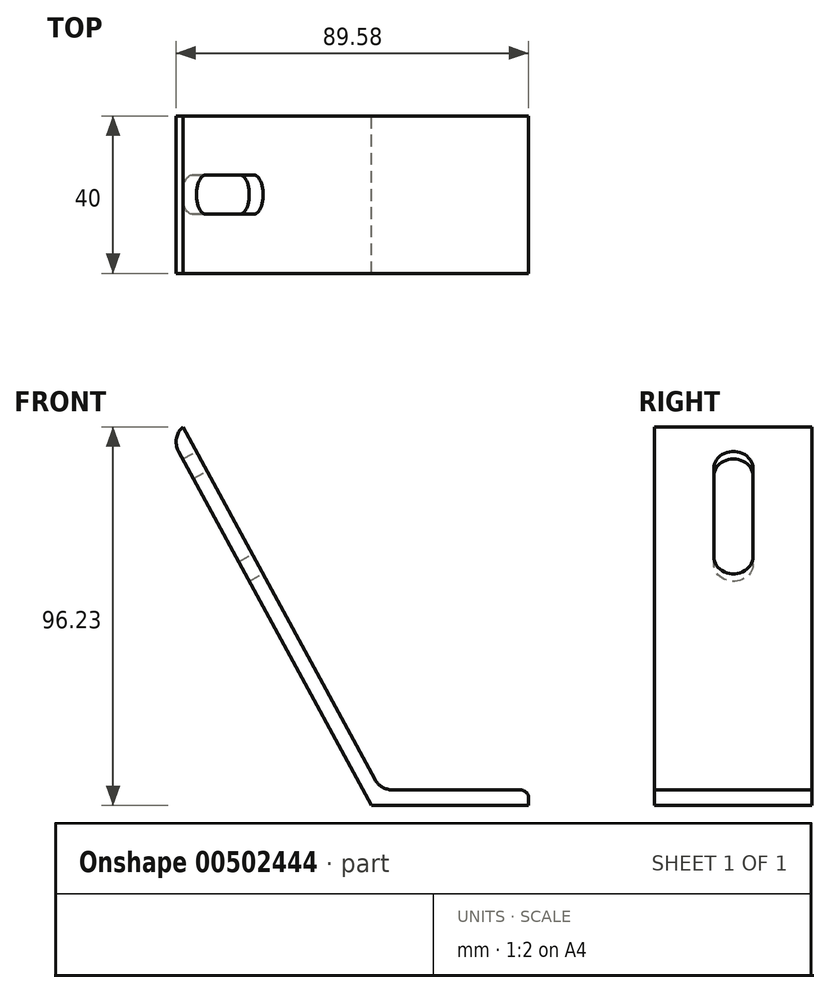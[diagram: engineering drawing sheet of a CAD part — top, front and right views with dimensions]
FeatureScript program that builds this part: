
annotation { "Feature Type Name" : "Feature", "Feature Type Description" : "" }
export const myFeature = defineFeature(function(context is Context, id is Id, definition is map)
    precondition{}
    {
        {
            var Q0;
            Q0=qCreatedBy(makeId("Front.planeOp"),FACE);
            var sketch = newSketch(context, id + "F0", { "sketchPlane" : qUnion([Q0])});
            skLineSegment(sketch, "E0", {"start": v(-3, 5.51) * mm, "end": v(-51.31, 94.32) * mm});
            skLineSegment(sketch, "E1", {"start": v(-51.31, 94.32) * mm, "end": v(-47.8, 96.23) * mm});
            skLineSegment(sketch, "E2", {"start": v(-47.8, 96.23) * mm, "end": v(2.38, 4) * mm});
            skLineSegment(sketch, "E3", {"start": v(2.38, 4) * mm, "end": v(40, 4) * mm});
            skLineSegment(sketch, "E4", {"start": v(40, 4) * mm, "end": v(40, 0) * mm});
            skLineSegment(sketch, "E5", {"start": v(40, 0) * mm, "end": v(0, 0) * mm});
            skLineSegment(sketch, "E6", {"start": v(0, 0) * mm, "end": v(-3, 5.51) * mm});
            skSolve(sketch);
        }
        {
            var Q0;
            Q0 = qSketchRegion(id + "F0", true);
            extrude(context, id + "F1", {"entities" : qUnion([Q0]), "depth" : 40 * mm});
        }
        {
            var Q0;
            Q0=makeQuery(id+"F1.opExtrude","SWEPT_EDGE",EDGE,{"disambiguationData":[OSD([sQuery(id+"F0.wireOp",EDGE,"E2"),sQuery(id+"F0.wireOp",EDGE,"E3")])]});
            var Q1;
            Q1=makeQuery(id+"F1.opExtrude","SWEPT_EDGE",EDGE,{"disambiguationData":[OSD([sQuery(id+"F0.wireOp",EDGE,"E0"),sQuery(id+"F0.wireOp",EDGE,"AraJsjXW-HaTJ-uxDT-Rq7w-RD12DYAYVZGL")])]});
            fillet(context, id + "F2", {"entities" : qUnion([Q0, Q1]), "radius" : 5 * mm, "tangentPropagation" : true, "allowEdgeOverflow" : false});
        }
        {
            var Q0;
            Q0=makeQuery(id+"F1.opExtrude","SWEPT_EDGE",EDGE,{"disambiguationData":[OSD([sQuery(id+"F0.wireOp",EDGE,"E3"),sQuery(id+"F0.wireOp",EDGE,"E4")])]});
            var Q1;
            Q1=makeQuery(id+"F1.opExtrude","SWEPT_EDGE",EDGE,{"disambiguationData":[OSD([sQuery(id+"F0.wireOp",EDGE,"jgJGadt5-KIKr-K8Ni-Qctq-57nrNfer92To"),sQuery(id+"F0.wireOp",EDGE,"jqPTAw02-jaw2-K15B-pJJS-fNdpXxf2ybxW")])]});
            var Q2;
            Q2=makeQuery(id+"F1.opExtrude","SWEPT_EDGE",EDGE,{"disambiguationData":[OSD([sQuery(id+"F0.wireOp",EDGE,"wX90dwEU-SlRl-KfoV-YeP7-xEuWKFcL9DTf"),sQuery(id+"F0.wireOp",EDGE,"AraJsjXW-HaTJ-uxDT-Rq7w-RD12DYAYVZGL")])]});
            var Q3;
            Q3=makeQuery(id+"F1.opExtrude","SWEPT_EDGE",EDGE,{"disambiguationData":[OSD([sQuery(id+"F0.wireOp",EDGE,"E1"),sQuery(id+"F0.wireOp",EDGE,"E2")])]});
            var Q4;
            Q4=makeQuery(id+"F1.opExtrude","SWEPT_EDGE",EDGE,{"disambiguationData":[OSD([sQuery(id+"F0.wireOp",EDGE,"E0"),sQuery(id+"F0.wireOp",EDGE,"E1")])]});
            fillet(context, id + "F3", {"entities" : qUnion([Q0, Q1, Q2, Q3, Q4]), "radius" : 2.17 * mm, "tangentPropagation" : true, "allowEdgeOverflow" : false});
        }
        {
            var Q0;
            Q0=makeQuery(id+"F1.opExtrude","SWEPT_FACE",FACE,{"disambiguationData":[OSD([sQuery(id+"F0.wireOp",EDGE,"E2")])]});
            var sketch = newSketch(context, id + "F4", { "sketchPlane" : qUnion([Q0])});
            skLineSegment(sketch, "E7", {"start": v(-20, 104.61) * mm, "end": v(-20, 51.26) * mm, "construction": true});
            skArc(sketch, "E8", {"start": v(-15, 95.26) * mm, "mid": v(-20.33, 100.25) * mm, "end": v(-24.96, 94.6) * mm});
            skArc(sketch, "E9", {"start": v(-24.96, 70.53) * mm, "mid": v(-20.33, 64.88) * mm, "end": v(-15, 69.86) * mm});
            skLineSegment(sketch, "E10", {"start": v(-24.96, 95.92) * mm, "end": v(-24.96, 70.53) * mm});
            skLineSegment(sketch, "E11", {"start": v(-15, 95.26) * mm, "end": v(-15, 69.86) * mm});
            skSolve(sketch);
        }
        {
            var Q0;
            Q0 = qSketchRegion(id + "F4", true);
            extrude(context, id + "F5", {"entities" : qUnion([Q0]), "operationType" : NewBodyOperationType.REMOVE, "oppositeDirection" : true, "depth" : 25 * mm});
        }
    });
